# Revit family: HC_Boiler_Condensate Flow_MEPcontent_De Dietrich Thermique_C 640 8-10_FR-FR
name_source: partatom
category: Mechanical Equipment
revit_build: Autodesk Revit 2018 (Build: 20170223_1515(x64)
units: mm (PartAtom-declared; Revit-internal decimal feet)

## family parameters
Always vertical = Yes
Classification = None
Cut with Voids When Loaded = No
OmniClass Number = 23.75.10.11.14
OmniClass Title = Hot Water Heat Generators
Part Type = Normal
Room Calculation Point = No
Round Connector Dimension = Use Diameter
Shared = No
Work Plane-Based = No

## types (3) — shared parameters
Access Clearance Front = 800 mm  [stored 2.62467 ft]
Access Clearance Left = 800 mm  [stored 2.62467 ft]
Access Clearance Rear = 300 mm  [stored 0.984252 ft]
Access Clearance Top = 450 mm  [stored 1.47638 ft]
Air Inlet Connection Size = 250 mm  [stored 0.82021 ft]
Base Family Version = 12.19
Blue = Color RGB 075-186-252
Condensate Drain Size = 32 mm  [stored 0.104987 ft]
Connection Placement = 129 mm  [stored 0.423228 ft]
Content Supplier URL = www.MEPcontent.com
Custom = No
Drain Connection Size = 20 mm  [stored 0.0656168 ft]
EMCS Version = 4.0
ETIM Article Class = EC010232
Family Version = 12.18
Flow and Return Connection Size = 80 mm  [stored 0.262467 ft]
Flue Connection Size = 350 mm  [stored 1.14829 ft]
Fuel Connection Size = 50 mm  [stored 0.164042 ft]
GLN = 8713809000004
Glass = Color RGB 218-227-224
Grey = Color RAL 7016
IFCExportAs = IfcBoiler
IFCExportType = NOTDEFINED
Light Gray = Color RGB 145-145-145
Logo = Color RGB 165-173-178
MEPcontent Class = BOILER_CONDENSATE_FLOW
Manufacturer = De Dietrich Thermique
Manufacturer URL = http://pro.dedietrich-thermique.fr
Overall Height = 1726 mm  [stored 5.66273 ft]
Overall Length = 2172 mm  [stored 7.12598 ft]
Overall Width = 1442 mm  [stored 4.73097 ft]
Phase = 1
Pipe Type Category = M561
Product Line = De Dietrich Thermique
Red = Color RAL 2002
Revit Version = 2018
Safety Valve Connection Size = 40 mm  [stored 0.131234 ft]
Safety Valve Diameter = 65 mm  [stored 0.213255 ft]
Supply Air Connection = 350 mm  [stored 1.14829 ft]
URL = https://mep.trimble.com
Use Nominal Diameter = Yes
Voltage = 230 V
White = Color RGB 219-219-219
Yellow = Color RGB 255-255-000
zero-valued in all types: Access Clearance Bottom, Access Clearance Right

## per-type parameters (varying)
| type | Article Description | Description | GTIN | Manufacturer Art. No. |
| 1000 | C 640 - 1000 | C 640 - 1000 | 8713809330279 | 7752876 |
| 1140 | C 640 - 1140 | C 640 - 1140 | 8713809330286 | 7752877 |
| 1300 | C 640 - 1300 | C 640 - 1300 | 8713809330293 | 7752878 |

note: column(s) folded — value = type name in every type: Article Type, Model

note: [stored X ft] marks values corroborated as IEEE doubles in the binary element streams (Revit-internal decimal feet)

## geometry (parser evidence)
native form markers: Sweep x17
no freeform markers — native parametric forms only
